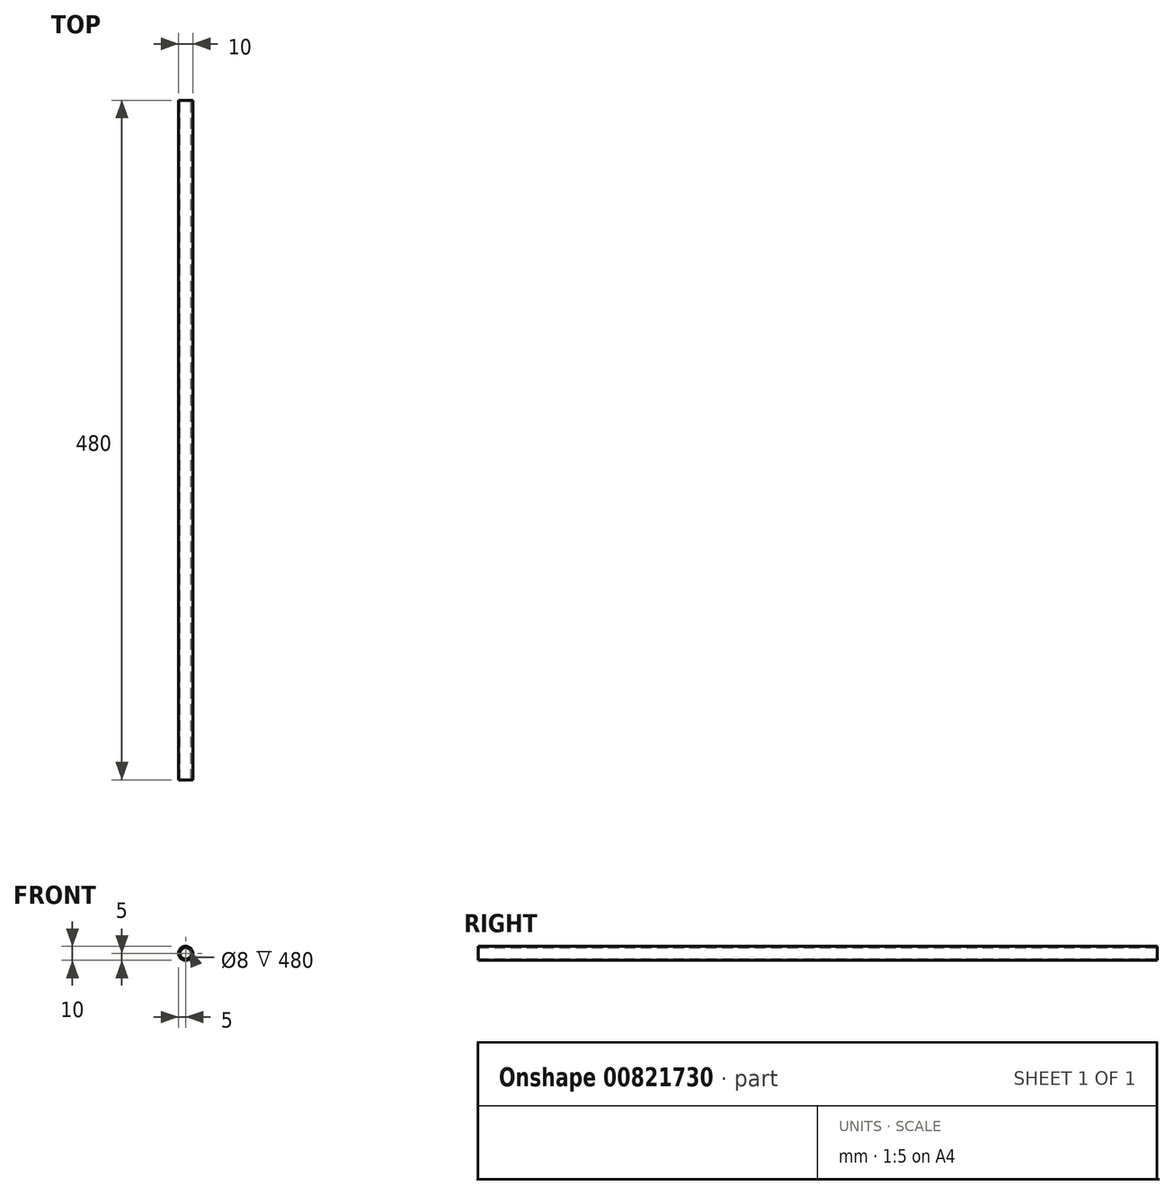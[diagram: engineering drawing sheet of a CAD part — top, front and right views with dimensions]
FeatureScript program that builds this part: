
annotation { "Feature Type Name" : "Feature", "Feature Type Description" : "" }
export const myFeature = defineFeature(function(context is Context, id is Id, definition is map)
    precondition{}
    {
        {
            var Q0;
            Q0=qCreatedBy(makeId("Front.planeOp"),FACE);
            var sketch = newSketch(context, id + "F0", { "sketchPlane" : qUnion([Q0])});
            skCircle(sketch, "E0", {"center": v(0, 0) * mm, "radius": 5 * mm});
            skCircle(sketch, "E1", {"center": v(0, 0) * mm, "radius": 4 * mm});
            skSolve(sketch);
        }
        {
            var Q0;
            Q0 = qSketchRegion(id + "F0", true);
            extrude(context, id + "F1", {"entities" : qUnion([Q0]), "depth" : 480 * mm, "offsetDistance" : 25 * mm});
        }
    });
